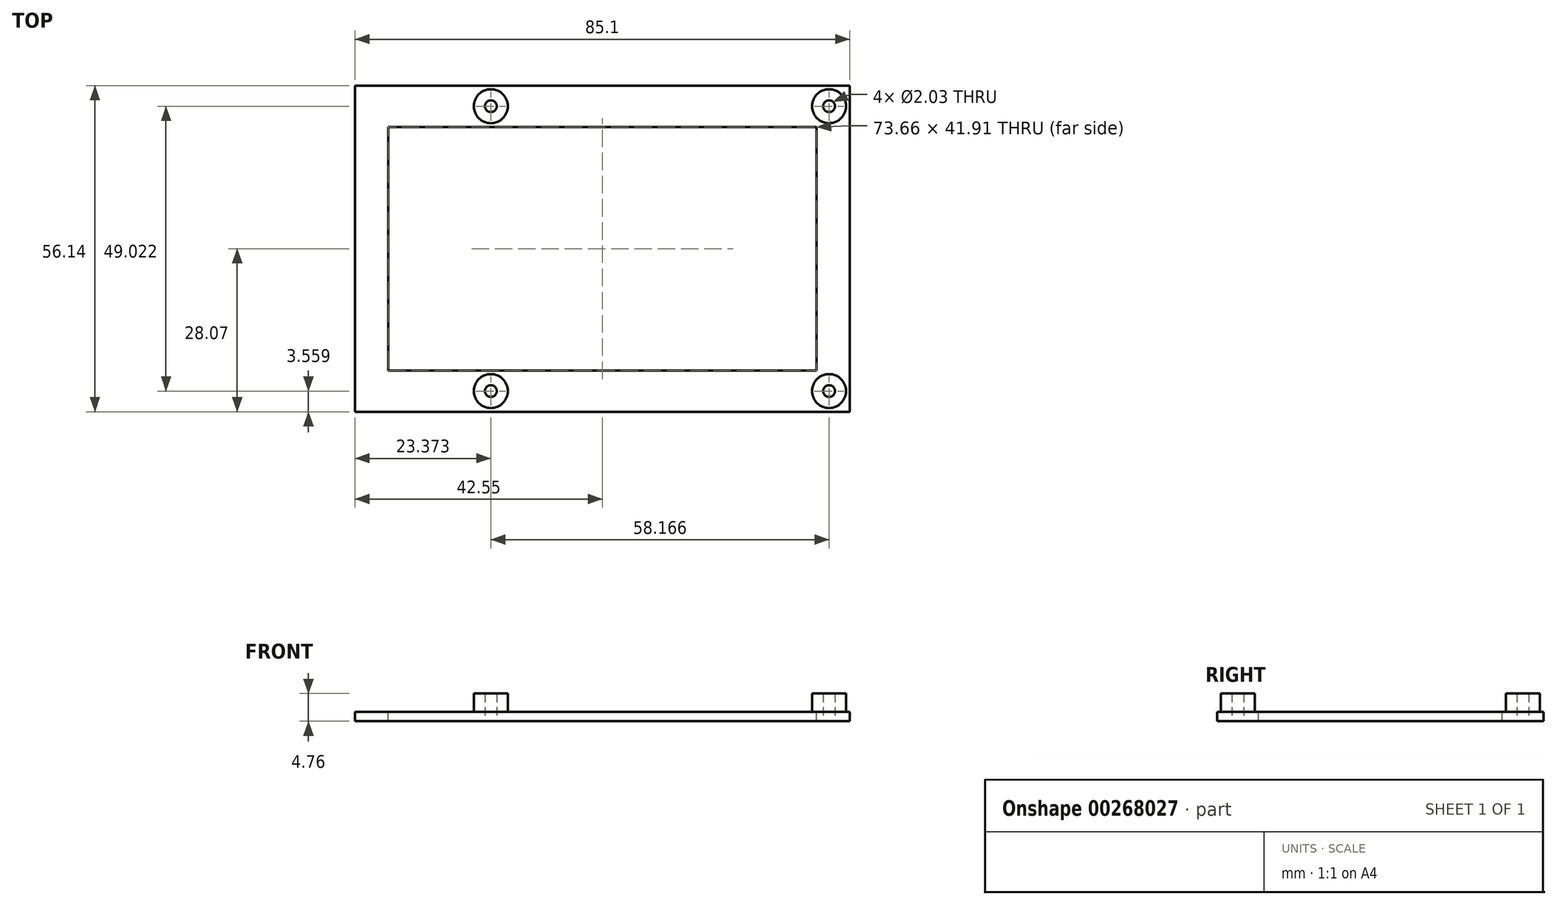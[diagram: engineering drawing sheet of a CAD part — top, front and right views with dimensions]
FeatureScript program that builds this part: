
annotation { "Feature Type Name" : "Feature", "Feature Type Description" : "" }
export const myFeature = defineFeature(function(context is Context, id is Id, definition is map)
    precondition{}
    {
        {
            var Q0;
            Q0=qCreatedBy(makeId("Top.planeOp"),FACE);
            var sketch = newSketch(context, id + "F0", { "sketchPlane" : qUnion([Q0])});
            skLineSegment(sketch, "E0.bottom", {"start": v(42.55, 28.07) * mm, "end": v(-42.55, 28.07) * mm});
            skLineSegment(sketch, "E0.top", {"start": v(42.55, -28.07) * mm, "end": v(-42.55, -28.07) * mm});
            skLineSegment(sketch, "E0.left", {"start": v(42.55, 28.07) * mm, "end": v(42.55, -28.07) * mm});
            skLineSegment(sketch, "E0.right", {"start": v(-42.55, 28.07) * mm, "end": v(-42.55, -28.07) * mm});
            skPoint(sketch, "E0.middle", {"position": v(0, 0) * mm});
            skSolve(sketch);
        }
        {
            var Q0;
            Q0=makeQuery(id+"F0.imprint","IMPRINT",FACE,{"disambiguationData":[TD([[makeQuery(id+"F0.imprint","IMPRINT",EDGE,{"derivedFrom":sQuery(id+"F0.wireOp",EDGE,"E0.bottom")}),1.0]])]});
            extrude(context, id + "F1", {"entities" : qUnion([Q0]), "depth" : 1.59 * mm});
        }
        {
            var Q0;
            Q0=makeQuery(id+"F1.opExtrude","CAP_FACE",FACE,{"disambiguationData":[OSD([sQuery(id+"F0.wireOp",EDGE,"E0.bottom"),sQuery(id+"F0.wireOp",EDGE,"E0.top"),sQuery(id+"F0.wireOp",EDGE,"E0.left"),sQuery(id+"F0.wireOp",EDGE,"E0.right")])],"isStart":false});
            var sketch = newSketch(context, id + "F2", { "sketchPlane" : qUnion([Q0])});
            skLineSegment(sketch, "E1.bottom", {"start": v(36.83, -20.96) * mm, "end": v(-36.83, -20.96) * mm});
            skLineSegment(sketch, "E1.top", {"start": v(36.83, 20.96) * mm, "end": v(-36.83, 20.96) * mm});
            skLineSegment(sketch, "E1.left", {"start": v(36.83, -20.96) * mm, "end": v(36.83, 20.96) * mm});
            skLineSegment(sketch, "E1.right", {"start": v(-36.83, -20.96) * mm, "end": v(-36.83, 20.95) * mm});
            skPoint(sketch, "E1.middle", {"position": v(0, 0) * mm});
            skSolve(sketch);
        }
        {
            var Q0;
            Q0=makeQuery(id+"F2.imprint","IMPRINT",FACE,{"disambiguationData":[TD([[makeQuery(id+"F2.imprint","IMPRINT",EDGE,{"derivedFrom":sQuery(id+"F2.wireOp",EDGE,"E1.bottom")}),-1.0]])]});
            extrude(context, id + "F3", {"entities" : qUnion([Q0]), "operationType" : NewBodyOperationType.REMOVE, "oppositeDirection" : true, "depth" : 6.35 * mm});
        }
        {
            var Q0;
            Q0=makeQuery(id+"F1.opExtrude","CAP_FACE",FACE,{"disambiguationData":[OSD([sQuery(id+"F0.wireOp",EDGE,"E0.bottom"),sQuery(id+"F0.wireOp",EDGE,"E0.top"),sQuery(id+"F0.wireOp",EDGE,"E0.left"),sQuery(id+"F0.wireOp",EDGE,"E0.right")])],"isStart":false});
            var sketch = newSketch(context, id + "F4", { "sketchPlane" : qUnion([Q0])});
            skLineSegment(sketch, "E2.bottom", {"start": v(38.99, -24.51) * mm, "end": v(42.55, -24.51) * mm, "construction": true});
            skLineSegment(sketch, "E2.top", {"start": v(38.99, -28.07) * mm, "end": v(42.55, -28.07) * mm, "construction": true});
            skLineSegment(sketch, "E2.left", {"start": v(38.99, -24.51) * mm, "end": v(38.99, -28.07) * mm, "construction": true});
            skLineSegment(sketch, "E2.right", {"start": v(42.55, -24.51) * mm, "end": v(42.55, -28.07) * mm, "construction": true});
            skCircle(sketch, "E3", {"center": v(38.99, -24.51) * mm, "radius": 1.02 * mm});
            skCircle(sketch, "E4", {"center": v(38.99, -24.51) * mm, "radius": 2.92 * mm});
            skLineSegment(sketch, "E5.bottom", {"start": v(38.99, -24.51) * mm, "end": v(-19.18, -24.51) * mm, "construction": true});
            skLineSegment(sketch, "E5.top", {"start": v(38.99, 24.51) * mm, "end": v(-19.18, 24.51) * mm, "construction": true});
            skLineSegment(sketch, "E5.left", {"start": v(38.99, -24.51) * mm, "end": v(38.99, 24.51) * mm, "construction": true});
            skLineSegment(sketch, "E5.right", {"start": v(-19.18, -24.51) * mm, "end": v(-19.18, 24.51) * mm, "construction": true});
            skCircle(sketch, "E6", {"center": v(-19.18, 24.51) * mm, "radius": 1.02 * mm});
            skCircle(sketch, "E7", {"center": v(-19.18, 24.51) * mm, "radius": 2.92 * mm});
            skCircle(sketch, "E8", {"center": v(38.99, 24.51) * mm, "radius": 1.02 * mm});
            skCircle(sketch, "E9", {"center": v(38.99, 24.51) * mm, "radius": 2.92 * mm});
            skCircle(sketch, "E10", {"center": v(-19.18, -24.51) * mm, "radius": 1.02 * mm});
            skCircle(sketch, "E11", {"center": v(-19.18, -24.51) * mm, "radius": 2.92 * mm});
            skLineSegment(sketch, "E12.bottom", {"start": v(42.55, -28.07) * mm, "end": v(-42.55, -28.07) * mm, "construction": true});
            skLineSegment(sketch, "E12.top", {"start": v(42.55, 28.07) * mm, "end": v(-42.55, 28.07) * mm, "construction": true});
            skLineSegment(sketch, "E12.left", {"start": v(42.55, -28.07) * mm, "end": v(42.55, 28.07) * mm, "construction": true});
            skLineSegment(sketch, "E12.right", {"start": v(-42.54, -28.07) * mm, "end": v(-42.54, 28.07) * mm, "construction": true});
            skSolve(sketch);
        }
        {
            var Q0;
            Q0=makeQuery(id+"F4.imprint","IMPRINT",FACE,{"disambiguationData":[TD([[makeQuery(id+"F4.imprint","IMPRINT",EDGE,{"derivedFrom":sQuery(id+"F4.wireOp",EDGE,"E8")}),-1.0]])]});
            var Q1;
            Q1=makeQuery(id+"F4.imprint","IMPRINT",FACE,{"disambiguationData":[TD([[makeQuery(id+"F4.imprint","IMPRINT",EDGE,{"derivedFrom":sQuery(id+"F4.wireOp",EDGE,"E3")}),-1.0]])]});
            var Q2;
            Q2=makeQuery(id+"F4.imprint","IMPRINT",FACE,{"disambiguationData":[TD([[makeQuery(id+"F4.imprint","IMPRINT",EDGE,{"derivedFrom":sQuery(id+"F4.wireOp",EDGE,"E6")}),-1.0]])]});
            var Q3;
            Q3=makeQuery(id+"F4.imprint","IMPRINT",FACE,{"disambiguationData":[TD([[makeQuery(id+"F4.imprint","IMPRINT",EDGE,{"derivedFrom":sQuery(id+"F4.wireOp",EDGE,"E10")}),-1.0]])]});
            extrude(context, id + "F5", {"entities" : qUnion([Q0, Q1, Q2, Q3]), "operationType" : NewBodyOperationType.ADD, "depth" : 3.17 * mm});
        }
        {
            var Q0;
            Q0=makeQuery(id+"F4.imprint","IMPRINT",FACE,{"disambiguationData":[TD([[makeQuery(id+"F4.imprint","IMPRINT",EDGE,{"derivedFrom":sQuery(id+"F4.wireOp",EDGE,"E3")}),1.0]])]});
            var Q1;
            Q1=makeQuery(id+"F4.imprint","IMPRINT",FACE,{"disambiguationData":[TD([[makeQuery(id+"F4.imprint","IMPRINT",EDGE,{"derivedFrom":sQuery(id+"F4.wireOp",EDGE,"E6")}),1.0]])]});
            var Q2;
            Q2=makeQuery(id+"F4.imprint","IMPRINT",FACE,{"disambiguationData":[TD([[makeQuery(id+"F4.imprint","IMPRINT",EDGE,{"derivedFrom":sQuery(id+"F4.wireOp",EDGE,"E8")}),1.0]])]});
            var Q3;
            Q3=makeQuery(id+"F4.imprint","IMPRINT",FACE,{"disambiguationData":[TD([[makeQuery(id+"F4.imprint","IMPRINT",EDGE,{"derivedFrom":sQuery(id+"F4.wireOp",EDGE,"E10")}),1.0]])]});
            extrude(context, id + "F6", {"entities" : qUnion([Q0, Q1, Q2, Q3]), "operationType" : NewBodyOperationType.REMOVE, "oppositeDirection" : true, "depth" : 6.35 * mm});
        }
    });
